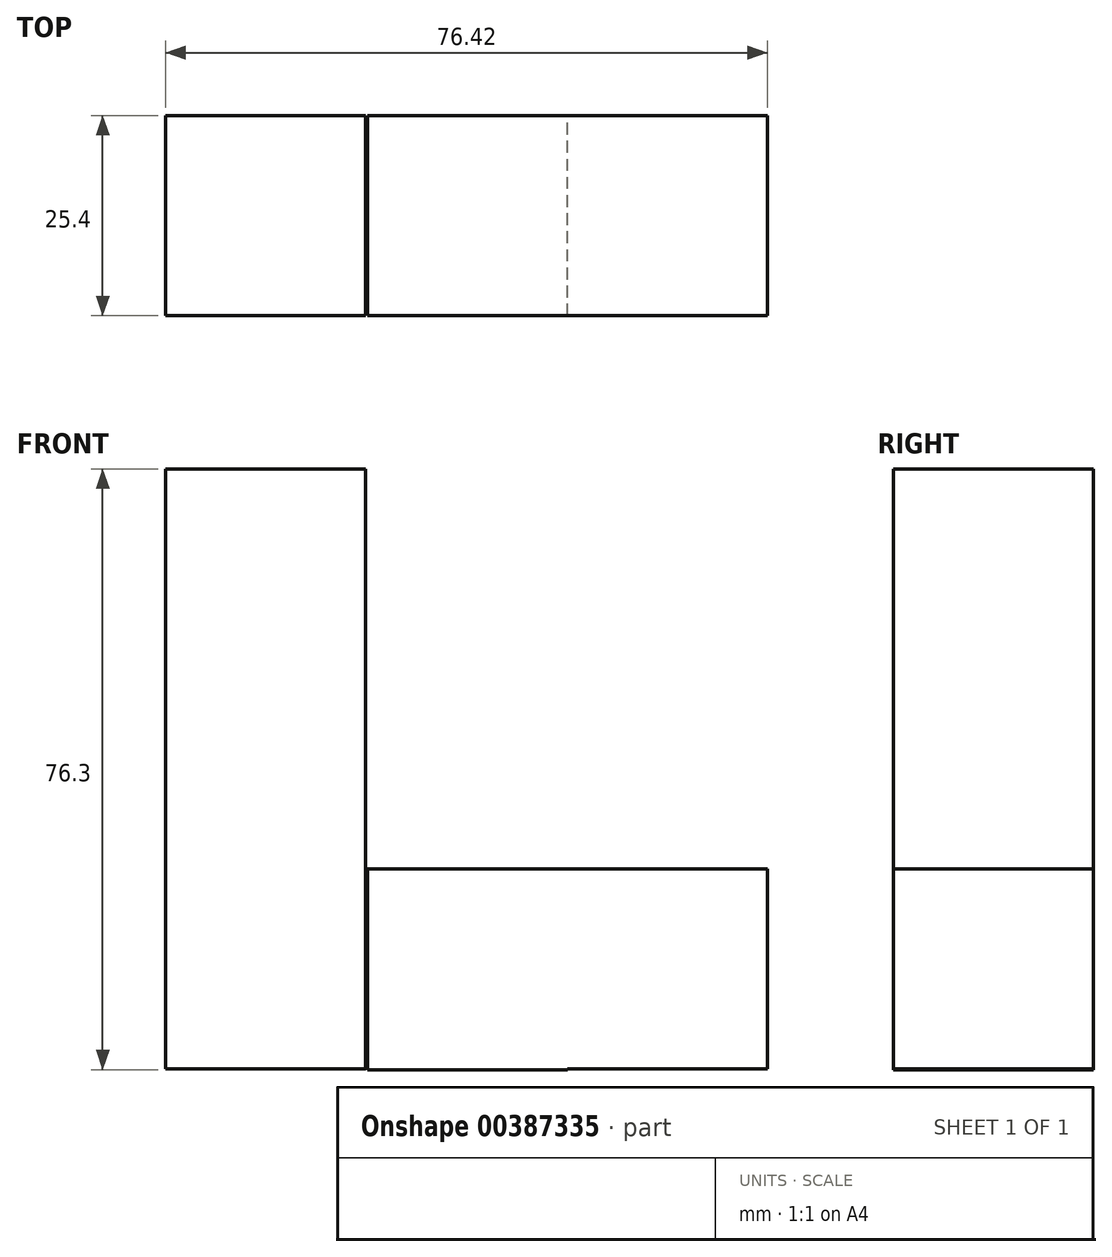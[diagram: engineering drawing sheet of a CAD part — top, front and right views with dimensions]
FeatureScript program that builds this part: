
annotation { "Feature Type Name" : "Feature", "Feature Type Description" : "" }
export const myFeature = defineFeature(function(context is Context, id is Id, definition is map)
    precondition{}
    {
        {
            var Q0;
            Q0=qCreatedBy(makeId("Front.planeOp"),FACE);
            var sketch = newSketch(context, id + "F0", { "sketchPlane" : qUnion([Q0])});
            skLineSegment(sketch, "E0.bottom", {"start": v(0, 0) * mm, "end": v(-25.4, 0) * mm});
            skLineSegment(sketch, "E0.top", {"start": v(0, -25.4) * mm, "end": v(-25.4, -25.4) * mm});
            skLineSegment(sketch, "E0.left", {"start": v(0, 0) * mm, "end": v(0, -25.4) * mm});
            skLineSegment(sketch, "E0.right", {"start": v(-25.4, 0) * mm, "end": v(-25.4, -25.4) * mm});
            skLineSegment(sketch, "E1.bottom", {"start": v(0.22, 0) * mm, "end": v(25.62, 0) * mm});
            skLineSegment(sketch, "E1.top", {"start": v(0.22, -25.5) * mm, "end": v(25.62, -25.5) * mm});
            skLineSegment(sketch, "E1.left", {"start": v(0.22, 0) * mm, "end": v(0.22, -25.5) * mm});
            skLineSegment(sketch, "E1.right", {"start": v(25.62, 0) * mm, "end": v(25.62, -25.5) * mm});
            skLineSegment(sketch, "E2.bottom", {"start": v(25.62, 0) * mm, "end": v(51.02, 0) * mm});
            skLineSegment(sketch, "E2.top", {"start": v(25.62, -25.4) * mm, "end": v(51.02, -25.4) * mm});
            skLineSegment(sketch, "E2.left", {"start": v(25.62, 0) * mm, "end": v(25.62, -25.4) * mm});
            skLineSegment(sketch, "E2.right", {"start": v(51.02, 0) * mm, "end": v(51.02, -25.4) * mm});
            skLineSegment(sketch, "E3.bottom", {"start": v(-25.4, 0) * mm, "end": v(0, 0) * mm});
            skLineSegment(sketch, "E3.top", {"start": v(-25.4, 25.4) * mm, "end": v(0, 25.4) * mm});
            skLineSegment(sketch, "E3.left", {"start": v(-25.4, 0) * mm, "end": v(-25.4, 25.4) * mm});
            skLineSegment(sketch, "E3.right", {"start": v(0, 0) * mm, "end": v(0, 25.4) * mm});
            skLineSegment(sketch, "E4.top", {"start": v(-25.4, 50.8) * mm, "end": v(0, 50.8) * mm});
            skLineSegment(sketch, "E4.left", {"start": v(-25.4, 25.4) * mm, "end": v(-25.4, 50.8) * mm});
            skLineSegment(sketch, "E4.right", {"start": v(0, 25.4) * mm, "end": v(0, 50.8) * mm});
            skSolve(sketch);
        }
        {
            var Q0;
            Q0 = qSketchRegion(id + "F0", true);
            extrude(context, id + "F1", {"entities" : qUnion([Q0]), "depth" : 25.4 * mm});
        }
    });
